# Revit family: BOS-Durchgangszarge-D-STW_Familie
name_source: partatom
category: Türen
revit_build: Autodesk Revit 2017 (Build: 20160225_1515(x64)
units: mm (PartAtom-declared; Revit-internal decimal feet)

## family parameters
Basisbauteil = Wand
Beim Laden mit Abzugskörper schneiden = Nein
Gemeinsam genutzt = Nein
Immer vertikal = Ja
Raumberechnungspunkt = Ja

## types (1)
- D
    Allgemeine Informationen zu Stahlzargen = www.BestOfSteel.de/tools-downloads/technische-infos-rund-um-die-stahlzarge/
    BE max. = 100 mm  [stored 0.328084 ft]
    Bauelement = BOS Stahlzarge
    Beschreibung = Durchgangszarge für Ständerwerk
    Breite = 0 mm  [stored 0 ft]
    D = Ja
    Dicke = 0 mm  [stored 0 ft]
    Einfügepunkt = 30 mm  [stored 0.0984252 ft]
    Funktion = Innen
    GT max. = 650 mm  [stored 2.13255 ft]
    Hersteller = BOS GmbH Best Of Steel, Lütkenfelde 4, D-48282 Emsdetten
    Info-Texte sichtbar = Ja
    Information in English = Nein
    LDB max. = 1311 mm  [stored 4.30118 ft]
    LDB min. = 561 mm
    LDH max. = 2843 mm  [stored 9.32743 ft]
    LDH min. = 1593 mm  [stored 5.22638 ft]
    MW max. = 620 mm
    MW min. = 100 mm  [stored 0.328084 ft]
    Material = grundiert, feuerverzinktes Feinblech nach DIN EN 10143
    Material - Zarge = <Nach Kategorie>
    Modell = D
    Putzwinkel hinten = 15 mm  [stored 0.0492126 ft]
    Putzwinkel vorne = 15 mm  [stored 0.0492126 ft]
    Rohbaubreite = 0 mm  [stored 0 ft]
    Rohbauhöhe = 0 mm  [stored 0 ft]
    Typenbild = <Keine Auswahl>
    URL = www.BestOfSteel.de/stahlzargen/weitere-loesungen/durchgangszargen/

note: [stored X ft] marks values corroborated as IEEE doubles in the binary element streams (Revit-internal decimal feet)
